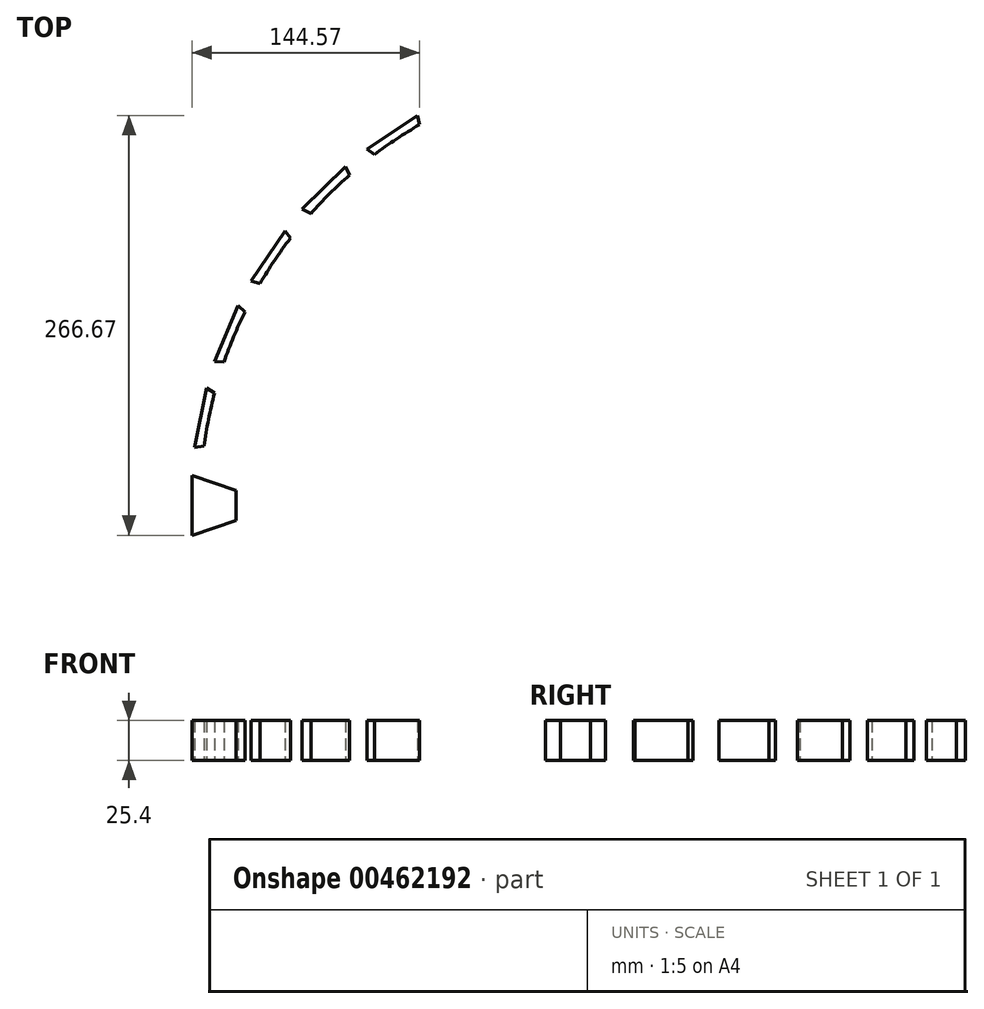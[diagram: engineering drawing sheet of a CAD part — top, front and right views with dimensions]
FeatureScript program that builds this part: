
annotation { "Feature Type Name" : "Feature", "Feature Type Description" : "" }
export const myFeature = defineFeature(function(context is Context, id is Id, definition is map)
    precondition{}
    {
        {
            var Q0;
            Q0=qCreatedBy(makeId("Top.planeOp"),FACE);
            var sketch = newSketch(context, id + "F0", { "sketchPlane" : qUnion([Q0])});
            skCircle(sketch, "E0", {"center": v(0, 0) * mm, "radius": 304.8 * mm});
            skCircle(sketch, "E1", {"center": v(0, 0) * mm, "radius": 279.4 * mm});
            skLineSegment(sketch, "E2", {"start": v(0, 0) * mm, "end": v(-514.18, 0) * mm, "construction": true});
            skLineSegment(sketch, "E3", {"start": v(-256.28, 9.5) * mm, "end": v(-284.48, 19.05) * mm});
            skLineSegment(sketch, "E4.MirrorCS", {"start": v(-256.12, -9.44) * mm, "end": v(-284.48, -19.05) * mm});
            skLineSegment(sketch, "E5", {"start": v(-284.48, 19.05) * mm, "end": v(-284.48, -19.05) * mm});
            skArc(sketch, "E6", {"start": v(-256.36, 9.53) * mm, "mid": v(-256.54, 0) * mm, "end": v(-256.36, -9.53) * mm});
            skLineSegment(sketch, "E7", {"start": v(-249.56, 59.5) * mm, "end": v(-275.26, 74.53) * mm});
            skLineSegment(sketch, "E8.MirrorCS", {"start": v(-253.6, 40.88) * mm, "end": v(-282.7, 36.77) * mm});
            skLineSegment(sketch, "E9", {"start": v(-249.56, 59.5) * mm, "end": v(-253.6, 40.88) * mm});
            skLineSegment(sketch, "E10", {"start": v(-275.26, 74.53) * mm, "end": v(-282.7, 36.77) * mm});
            skLineSegment(sketch, "E11", {"start": v(-278.98, 55.65) * mm, "end": v(0, 0) * mm, "construction": true});
            skLineSegment(sketch, "E12", {"start": v(-233.4, 107.28) * mm, "end": v(-255.29, 126.9) * mm});
            skLineSegment(sketch, "E13.MirrorCS", {"start": v(-240.41, 89.57) * mm, "end": v(-270.13, 91.4) * mm});
            skLineSegment(sketch, "E14", {"start": v(-233.4, 107.28) * mm, "end": v(-240.41, 89.57) * mm});
            skLineSegment(sketch, "E15", {"start": v(-255.29, 126.9) * mm, "end": v(-270.13, 91.4) * mm});
            skLineSegment(sketch, "E16", {"start": v(0, 0) * mm, "end": v(-262.7, 109.15) * mm, "construction": true});
            skLineSegment(sketch, "E17", {"start": v(-207.9, 150.87) * mm, "end": v(-225.53, 174.38) * mm});
            skLineSegment(sketch, "E18.MirrorCS", {"start": v(-218.25, 134.87) * mm, "end": v(-247.03, 142.47) * mm});
            skLineSegment(sketch, "E19", {"start": v(-207.9, 150.87) * mm, "end": v(-218.25, 134.87) * mm});
            skLineSegment(sketch, "E20", {"start": v(-225.53, 174.38) * mm, "end": v(-247.03, 142.47) * mm});
            skLineSegment(sketch, "E21", {"start": v(0, 0) * mm, "end": v(-236.28, 158.43) * mm, "construction": true});
            skLineSegment(sketch, "E22", {"start": v(-251.58, 50.18) * mm, "end": v(0, 0) * mm, "construction": true});
            skLineSegment(sketch, "E23", {"start": v(0, 0) * mm, "end": v(-236.9, 98.43) * mm, "construction": true});
            skLineSegment(sketch, "E24", {"start": v(0, 0) * mm, "end": v(-213.08, 142.87) * mm, "construction": true});
            skLineSegment(sketch, "E25", {"start": v(-174.64, 188.87) * mm, "end": v(-187, 215.06) * mm});
            skLineSegment(sketch, "E26.MirrorCS", {"start": v(-187.38, 174.71) * mm, "end": v(-214.45, 188.13) * mm});
            skLineSegment(sketch, "E27", {"start": v(-174.64, 188.87) * mm, "end": v(-187.38, 174.71) * mm});
            skLineSegment(sketch, "E28", {"start": v(-187, 215.06) * mm, "end": v(-214.45, 188.13) * mm});
            skLineSegment(sketch, "E29", {"start": v(0, 0) * mm, "end": v(-200.73, 201.6) * mm, "construction": true});
            skLineSegment(sketch, "E30", {"start": v(0, 0) * mm, "end": v(-181.01, 181.79) * mm, "construction": true});
            skLineSegment(sketch, "E31", {"start": v(-133.99, 218.9) * mm, "end": v(-141.4, 247.62) * mm});
            skLineSegment(sketch, "E32.MirrorCS", {"start": v(-149.92, 208.46) * mm, "end": v(-173.43, 226.3) * mm});
            skLineSegment(sketch, "E33", {"start": v(-133.99, 218.9) * mm, "end": v(-149.92, 208.46) * mm});
            skLineSegment(sketch, "E34", {"start": v(-141.4, 247.62) * mm, "end": v(-173.43, 226.3) * mm});
            skLineSegment(sketch, "E35", {"start": v(0, 0) * mm, "end": v(-157.41, 236.96) * mm, "construction": true});
            skLineSegment(sketch, "E36", {"start": v(0, 0) * mm, "end": v(-141.95, 213.69) * mm, "construction": true});
            skLineSegment(sketch, "E37", {"start": v(0, 0) * mm, "end": v(-304.8, 0) * mm, "construction": true});
            skPoint(sketch, "E38.orphan", {"position": v(-256.36, 9.53) * mm});
            skPoint(sketch, "E39.orphan", {"position": v(-256.36, -9.53) * mm});
            skArc(sketch, "E40.trimOffspring", {"start": v(-139.42, 215.35) * mm, "mid": v(-140.7, 214.52) * mm, "end": v(-141.95, 213.69) * mm});
            skArc(sketch, "E41.trimOffspring", {"start": v(-249.74, 58.67) * mm, "mid": v(-250.7, 54.43) * mm, "end": v(-251.58, 50.18) * mm});
            skArc(sketch, "E42.trimOffspring", {"start": v(-236.9, 98.43) * mm, "mid": v(-238.54, 94.4) * mm, "end": v(-240.1, 90.36) * mm});
            skArc(sketch, "E43.trimOffspring", {"start": v(-213.08, 142.87) * mm, "mid": v(-215.4, 139.34) * mm, "end": v(-217.67, 135.77) * mm});
            skArc(sketch, "E44.trimOffspring", {"start": v(-181.01, 181.79) * mm, "mid": v(-184.4, 178.36) * mm, "end": v(-187.7, 174.87) * mm});
            skSolve(sketch);
        }
        {
            var Q0;
            Q0=makeQuery(id+"F0.imprint","IMPRINT",FACE,{"disambiguationData":[TD([[makeQuery(id+"F0.imprint","IMPRINT",EDGE,{"derivedFrom":sQuery(id+"F0.wireOp",EDGE,"E0")}),-1.0]])]});
            var Q1;
            {var subQ5=sQuery(id+"F0.wireOp",EDGE,"E20");Q1=makeQuery(id+"F0.imprint","IMPRINT",FACE,{"disambiguationData":[TD([[makeQuery(id+"F0.imprint","IMPRINT",EDGE,{"derivedFrom":subQ5}),1.0]])]});}
            var Q2;
            {var subQ5=sQuery(id+"F0.wireOp",EDGE,"E28");Q2=makeQuery(id+"F0.imprint","IMPRINT",FACE,{"disambiguationData":[TD([[makeQuery(id+"F0.imprint","IMPRINT",EDGE,{"derivedFrom":subQ5}),1.0]])]});}
            var Q3;
            {var subQ5=sQuery(id+"F0.wireOp",EDGE,"E34");Q3=makeQuery(id+"F0.imprint","IMPRINT",FACE,{"disambiguationData":[TD([[makeQuery(id+"F0.imprint","IMPRINT",EDGE,{"derivedFrom":subQ5}),1.0]])]});}
            var Q4;
            {var subQ5=sQuery(id+"F0.wireOp",EDGE,"E15");Q4=makeQuery(id+"F0.imprint","IMPRINT",FACE,{"disambiguationData":[TD([[makeQuery(id+"F0.imprint","IMPRINT",EDGE,{"derivedFrom":subQ5}),1.0]])]});}
            var Q5;
            {var subQ5=sQuery(id+"F0.wireOp",EDGE,"E10");Q5=makeQuery(id+"F0.imprint","IMPRINT",FACE,{"disambiguationData":[TD([[makeQuery(id+"F0.imprint","IMPRINT",EDGE,{"derivedFrom":subQ5}),1.0]])]});}
            var Q6;
            {var subQ5=sQuery(id+"F0.wireOp",EDGE,"E5");Q6=makeQuery(id+"F0.imprint","IMPRINT",FACE,{"disambiguationData":[TD([[makeQuery(id+"F0.imprint","IMPRINT",EDGE,{"derivedFrom":subQ5}),1.0]])]});}
            extrude(context, id + "F1", {"entities" : qUnion([Q0, Q1, Q2, Q3, Q4, Q5, Q6]), "depth" : 25.4 * mm});
        }
        {
            var Q0;
            {var subQ5=sQuery(id+"F0.wireOp",EDGE,"E6");Q0=makeQuery(id+"F0.imprint","IMPRINT",FACE,{"disambiguationData":[TD([[makeQuery(id+"F0.imprint","IMPRINT",EDGE,{"derivedFrom":subQ5}),-1.0]])]});}
            extrude(context, id + "F2", {"entities" : qUnion([Q0]), "operationType" : NewBodyOperationType.ADD, "depth" : 25.4 * mm});
        }
        {
            var Q0;
            {var subQ0=sQuery(id+"F0.wireOp",EDGE,"E6");var subQ1=sQuery(id+"F0.wireOp",EDGE,"E4.MirrorCS");var subQ2=sQuery(id+"F0.wireOp",EDGE,"E3");var subQ3=sQuery(id+"F0.wireOp",EDGE,"E1");Q0=makeQuery(id+"Fd8F3SVLfFubU3N_1.31.F2.boolean.opBoolean","MERGE",FACE,{"derivedFrom":[makeQuery(id+"Fd8F3SVLfFubU3N_1.30.F2.boolean.opBoolean","MERGE",FACE,{"derivedFrom":[makeQuery(id+"Fd8F3SVLfFubU3N_1.29.F2.boolean.opBoolean","MERGE",FACE,{"derivedFrom":[makeQuery(id+"Fd8F3SVLfFubU3N_1.28.F2.boolean.opBoolean","MERGE",FACE,{"derivedFrom":[makeQuery(id+"Fd8F3SVLfFubU3N_1.27.F2.boolean.opBoolean","MERGE",FACE,{"derivedFrom":[makeQuery(id+"Fd8F3SVLfFubU3N_1.26.F2.boolean.opBoolean","MERGE",FACE,{"derivedFrom":[makeQuery(id+"Fd8F3SVLfFubU3N_1.25.F2.boolean.opBoolean","MERGE",FACE,{"derivedFrom":[makeQuery(id+"Fd8F3SVLfFubU3N_1.24.F2.boolean.opBoolean","MERGE",FACE,{"derivedFrom":[makeQuery(id+"Fd8F3SVLfFubU3N_1.23.F2.boolean.opBoolean","MERGE",FACE,{"derivedFrom":[makeQuery(id+"Fd8F3SVLfFubU3N_1.22.F2.boolean.opBoolean","MERGE",FACE,{"derivedFrom":[makeQuery(id+"Fd8F3SVLfFubU3N_1.21.F2.boolean.opBoolean","MERGE",FACE,{"derivedFrom":[makeQuery(id+"Fd8F3SVLfFubU3N_1.20.F2.boolean.opBoolean","MERGE",FACE,{"derivedFrom":[makeQuery(id+"Fd8F3SVLfFubU3N_1.19.F2.boolean.opBoolean","MERGE",FACE,{"derivedFrom":[makeQuery(id+"Fd8F3SVLfFubU3N_1.18.F2.boolean.opBoolean","MERGE",FACE,{"derivedFrom":[makeQuery(id+"Fd8F3SVLfFubU3N_1.17.F2.boolean.opBoolean","MERGE",FACE,{"derivedFrom":[makeQuery(id+"Fd8F3SVLfFubU3N_1.16.F2.boolean.opBoolean","MERGE",FACE,{"derivedFrom":[makeQuery(id+"Fd8F3SVLfFubU3N_1.15.F2.boolean.opBoolean","MERGE",FACE,{"derivedFrom":[makeQuery(id+"Fd8F3SVLfFubU3N_1.14.F2.boolean.opBoolean","MERGE",FACE,{"derivedFrom":[makeQuery(id+"Fd8F3SVLfFubU3N_1.13.F2.boolean.opBoolean","MERGE",FACE,{"derivedFrom":[makeQuery(id+"Fd8F3SVLfFubU3N_1.12.F2.boolean.opBoolean","MERGE",FACE,{"derivedFrom":[makeQuery(id+"Fd8F3SVLfFubU3N_1.11.F2.boolean.opBoolean","MERGE",FACE,{"derivedFrom":[makeQuery(id+"Fd8F3SVLfFubU3N_1.10.F2.boolean.opBoolean","MERGE",FACE,{"derivedFrom":[makeQuery(id+"Fd8F3SVLfFubU3N_1.9.F2.boolean.opBoolean","MERGE",FACE,{"derivedFrom":[makeQuery(id+"Fd8F3SVLfFubU3N_1.8.F2.boolean.opBoolean","MERGE",FACE,{"derivedFrom":[makeQuery(id+"Fd8F3SVLfFubU3N_1.7.F2.boolean.opBoolean","MERGE",FACE,{"derivedFrom":[makeQuery(id+"Fd8F3SVLfFubU3N_1.6.F2.boolean.opBoolean","MERGE",FACE,{"derivedFrom":[makeQuery(id+"Fd8F3SVLfFubU3N_1.5.F2.boolean.opBoolean","MERGE",FACE,{"derivedFrom":[makeQuery(id+"Fd8F3SVLfFubU3N_1.4.F2.boolean.opBoolean","MERGE",FACE,{"derivedFrom":[makeQuery(id+"Fd8F3SVLfFubU3N_1.3.F2.boolean.opBoolean","MERGE",FACE,{"derivedFrom":[makeQuery(id+"Fd8F3SVLfFubU3N_1.2.F2.boolean.opBoolean","MERGE",FACE,{"derivedFrom":[makeQuery(id+"Fd8F3SVLfFubU3N_1.1.F2.boolean.opBoolean","MERGE",FACE,{"derivedFrom":[makeQuery(id+"F2.boolean.opBoolean","MERGE",FACE,{"derivedFrom":[makeQuery(id+"F1.opExtrude","CAP_FACE",FACE,{"disambiguationData":[OSD([subQ3,sQuery(id+"F0.wireOp",EDGE,"E0")])],"isStart":true}),makeQuery(id+"F2.opExtrude","CAP_FACE",FACE,{"disambiguationData":[OSD([subQ3,subQ2,subQ1,subQ0])],"isStart":true})]}),makeQuery(id+"Fd8F3SVLfFubU3N_1.1.F2.opExtrude","CAP_FACE",FACE,{"disambiguationData":[OSD([subQ3,subQ2,subQ1,subQ0])],"isStart":true})]}),makeQuery(id+"Fd8F3SVLfFubU3N_1.2.F2.opExtrude","CAP_FACE",FACE,{"disambiguationData":[OSD([subQ3,subQ2,subQ1,subQ0])],"isStart":true})]}),makeQuery(id+"Fd8F3SVLfFubU3N_1.3.F2.opExtrude","CAP_FACE",FACE,{"disambiguationData":[OSD([subQ3,subQ2,subQ1,subQ0])],"isStart":true})]}),makeQuery(id+"Fd8F3SVLfFubU3N_1.4.F2.opExtrude","CAP_FACE",FACE,{"disambiguationData":[OSD([subQ3,subQ2,subQ1,subQ0])],"isStart":true})]}),makeQuery(id+"Fd8F3SVLfFubU3N_1.5.F2.opExtrude","CAP_FACE",FACE,{"disambiguationData":[OSD([subQ3,subQ2,subQ1,subQ0])],"isStart":true})]}),makeQuery(id+"Fd8F3SVLfFubU3N_1.6.F2.opExtrude","CAP_FACE",FACE,{"disambiguationData":[OSD([subQ3,subQ2,subQ1,subQ0])],"isStart":true})]}),makeQuery(id+"Fd8F3SVLfFubU3N_1.7.F2.opExtrude","CAP_FACE",FACE,{"disambiguationData":[OSD([subQ3,subQ2,subQ1,subQ0])],"isStart":true})]}),makeQuery(id+"Fd8F3SVLfFubU3N_1.8.F2.opExtrude","CAP_FACE",FACE,{"disambiguationData":[OSD([subQ3,subQ2,subQ1,subQ0])],"isStart":true})]}),makeQuery(id+"Fd8F3SVLfFubU3N_1.9.F2.opExtrude","CAP_FACE",FACE,{"disambiguationData":[OSD([subQ3,subQ2,subQ1,subQ0])],"isStart":true})]}),makeQuery(id+"Fd8F3SVLfFubU3N_1.10.F2.opExtrude","CAP_FACE",FACE,{"disambiguationData":[OSD([subQ3,subQ2,subQ1,subQ0])],"isStart":true})]}),makeQuery(id+"Fd8F3SVLfFubU3N_1.11.F2.opExtrude","CAP_FACE",FACE,{"disambiguationData":[OSD([subQ3,subQ2,subQ1,subQ0])],"isStart":true})]}),makeQuery(id+"Fd8F3SVLfFubU3N_1.12.F2.opExtrude","CAP_FACE",FACE,{"disambiguationData":[OSD([subQ3,subQ2,subQ1,subQ0])],"isStart":true})]}),makeQuery(id+"Fd8F3SVLfFubU3N_1.13.F2.opExtrude","CAP_FACE",FACE,{"disambiguationData":[OSD([subQ3,subQ2,subQ1,subQ0])],"isStart":true})]}),makeQuery(id+"Fd8F3SVLfFubU3N_1.14.F2.opExtrude","CAP_FACE",FACE,{"disambiguationData":[OSD([subQ3,subQ2,subQ1,subQ0])],"isStart":true})]}),makeQuery(id+"Fd8F3SVLfFubU3N_1.15.F2.opExtrude","CAP_FACE",FACE,{"disambiguationData":[OSD([subQ3,subQ2,subQ1,subQ0])],"isStart":true})]}),makeQuery(id+"Fd8F3SVLfFubU3N_1.16.F2.opExtrude","CAP_FACE",FACE,{"disambiguationData":[OSD([subQ3,subQ2,subQ1,subQ0])],"isStart":true})]}),makeQuery(id+"Fd8F3SVLfFubU3N_1.17.F2.opExtrude","CAP_FACE",FACE,{"disambiguationData":[OSD([subQ3,subQ2,subQ1,subQ0])],"isStart":true})]}),makeQuery(id+"Fd8F3SVLfFubU3N_1.18.F2.opExtrude","CAP_FACE",FACE,{"disambiguationData":[OSD([subQ3,subQ2,subQ1,subQ0])],"isStart":true})]}),makeQuery(id+"Fd8F3SVLfFubU3N_1.19.F2.opExtrude","CAP_FACE",FACE,{"disambiguationData":[OSD([subQ3,subQ2,subQ1,subQ0])],"isStart":true})]}),makeQuery(id+"Fd8F3SVLfFubU3N_1.20.F2.opExtrude","CAP_FACE",FACE,{"disambiguationData":[OSD([subQ3,subQ2,subQ1,subQ0])],"isStart":true})]}),makeQuery(id+"Fd8F3SVLfFubU3N_1.21.F2.opExtrude","CAP_FACE",FACE,{"disambiguationData":[OSD([subQ3,subQ2,subQ1,subQ0])],"isStart":true})]}),makeQuery(id+"Fd8F3SVLfFubU3N_1.22.F2.opExtrude","CAP_FACE",FACE,{"disambiguationData":[OSD([subQ3,subQ2,subQ1,subQ0])],"isStart":true})]}),makeQuery(id+"Fd8F3SVLfFubU3N_1.23.F2.opExtrude","CAP_FACE",FACE,{"disambiguationData":[OSD([subQ3,subQ2,subQ1,subQ0])],"isStart":true})]}),makeQuery(id+"Fd8F3SVLfFubU3N_1.24.F2.opExtrude","CAP_FACE",FACE,{"disambiguationData":[OSD([subQ3,subQ2,subQ1,subQ0])],"isStart":true})]}),makeQuery(id+"Fd8F3SVLfFubU3N_1.25.F2.opExtrude","CAP_FACE",FACE,{"disambiguationData":[OSD([subQ3,subQ2,subQ1,subQ0])],"isStart":true})]}),makeQuery(id+"Fd8F3SVLfFubU3N_1.26.F2.opExtrude","CAP_FACE",FACE,{"disambiguationData":[OSD([subQ3,subQ2,subQ1,subQ0])],"isStart":true})]}),makeQuery(id+"Fd8F3SVLfFubU3N_1.27.F2.opExtrude","CAP_FACE",FACE,{"disambiguationData":[OSD([subQ3,subQ2,subQ1,subQ0])],"isStart":true})]}),makeQuery(id+"Fd8F3SVLfFubU3N_1.28.F2.opExtrude","CAP_FACE",FACE,{"disambiguationData":[OSD([subQ3,subQ2,subQ1,subQ0])],"isStart":true})]}),makeQuery(id+"Fd8F3SVLfFubU3N_1.29.F2.opExtrude","CAP_FACE",FACE,{"disambiguationData":[OSD([subQ3,subQ2,subQ1,subQ0])],"isStart":true})]}),makeQuery(id+"Fd8F3SVLfFubU3N_1.30.F2.opExtrude","CAP_FACE",FACE,{"disambiguationData":[OSD([subQ3,subQ2,subQ1,subQ0])],"isStart":true})]}),makeQuery(id+"Fd8F3SVLfFubU3N_1.31.F2.opExtrude","CAP_FACE",FACE,{"disambiguationData":[OSD([subQ3,subQ2,subQ1,subQ0])],"isStart":true})]});}
            var sketch = newSketch(context, id + "F3", { "sketchPlane" : qUnion([Q0])});
            skCircle(sketch, "E45", {"center": v(0, 0) * mm, "radius": 296.86 * mm});
            skCircle(sketch, "E46", {"center": v(0, 0) * mm, "radius": 290.51 * mm});
            skSolve(sketch);
        }
        {
            var Q0;
            Q0=makeQuery(id+"F3.imprint","IMPRINT",FACE,{"disambiguationData":[TD([[makeQuery(id+"F3.imprint","IMPRINT",EDGE,{"derivedFrom":sQuery(id+"F3.wireOp",EDGE,"E45")}),1.0]])]});
            extrude(context, id + "F4", {"entities" : qUnion([Q0]), "operationType" : NewBodyOperationType.REMOVE, "oppositeDirection" : true, "depth" : 2.54 * mm});
        }
        {
            var Q0;
            {var subQ0=sQuery(id+"F0.wireOp",EDGE,"E6");var subQ1=sQuery(id+"F0.wireOp",EDGE,"E4.MirrorCS");var subQ2=sQuery(id+"F0.wireOp",EDGE,"E3");var subQ3=sQuery(id+"F0.wireOp",EDGE,"E1");Q0=makeQuery(id+"Fd8F3SVLfFubU3N_1.31.F2.boolean.opBoolean","MERGE",FACE,{"derivedFrom":[makeQuery(id+"Fd8F3SVLfFubU3N_1.30.F2.boolean.opBoolean","MERGE",FACE,{"derivedFrom":[makeQuery(id+"Fd8F3SVLfFubU3N_1.29.F2.boolean.opBoolean","MERGE",FACE,{"derivedFrom":[makeQuery(id+"Fd8F3SVLfFubU3N_1.28.F2.boolean.opBoolean","MERGE",FACE,{"derivedFrom":[makeQuery(id+"Fd8F3SVLfFubU3N_1.27.F2.boolean.opBoolean","MERGE",FACE,{"derivedFrom":[makeQuery(id+"Fd8F3SVLfFubU3N_1.26.F2.boolean.opBoolean","MERGE",FACE,{"derivedFrom":[makeQuery(id+"Fd8F3SVLfFubU3N_1.25.F2.boolean.opBoolean","MERGE",FACE,{"derivedFrom":[makeQuery(id+"Fd8F3SVLfFubU3N_1.24.F2.boolean.opBoolean","MERGE",FACE,{"derivedFrom":[makeQuery(id+"Fd8F3SVLfFubU3N_1.23.F2.boolean.opBoolean","MERGE",FACE,{"derivedFrom":[makeQuery(id+"Fd8F3SVLfFubU3N_1.22.F2.boolean.opBoolean","MERGE",FACE,{"derivedFrom":[makeQuery(id+"Fd8F3SVLfFubU3N_1.21.F2.boolean.opBoolean","MERGE",FACE,{"derivedFrom":[makeQuery(id+"Fd8F3SVLfFubU3N_1.20.F2.boolean.opBoolean","MERGE",FACE,{"derivedFrom":[makeQuery(id+"Fd8F3SVLfFubU3N_1.19.F2.boolean.opBoolean","MERGE",FACE,{"derivedFrom":[makeQuery(id+"Fd8F3SVLfFubU3N_1.18.F2.boolean.opBoolean","MERGE",FACE,{"derivedFrom":[makeQuery(id+"Fd8F3SVLfFubU3N_1.17.F2.boolean.opBoolean","MERGE",FACE,{"derivedFrom":[makeQuery(id+"Fd8F3SVLfFubU3N_1.16.F2.boolean.opBoolean","MERGE",FACE,{"derivedFrom":[makeQuery(id+"Fd8F3SVLfFubU3N_1.15.F2.boolean.opBoolean","MERGE",FACE,{"derivedFrom":[makeQuery(id+"Fd8F3SVLfFubU3N_1.14.F2.boolean.opBoolean","MERGE",FACE,{"derivedFrom":[makeQuery(id+"Fd8F3SVLfFubU3N_1.13.F2.boolean.opBoolean","MERGE",FACE,{"derivedFrom":[makeQuery(id+"Fd8F3SVLfFubU3N_1.12.F2.boolean.opBoolean","MERGE",FACE,{"derivedFrom":[makeQuery(id+"Fd8F3SVLfFubU3N_1.11.F2.boolean.opBoolean","MERGE",FACE,{"derivedFrom":[makeQuery(id+"Fd8F3SVLfFubU3N_1.10.F2.boolean.opBoolean","MERGE",FACE,{"derivedFrom":[makeQuery(id+"Fd8F3SVLfFubU3N_1.9.F2.boolean.opBoolean","MERGE",FACE,{"derivedFrom":[makeQuery(id+"Fd8F3SVLfFubU3N_1.8.F2.boolean.opBoolean","MERGE",FACE,{"derivedFrom":[makeQuery(id+"Fd8F3SVLfFubU3N_1.7.F2.boolean.opBoolean","MERGE",FACE,{"derivedFrom":[makeQuery(id+"Fd8F3SVLfFubU3N_1.6.F2.boolean.opBoolean","MERGE",FACE,{"derivedFrom":[makeQuery(id+"Fd8F3SVLfFubU3N_1.5.F2.boolean.opBoolean","MERGE",FACE,{"derivedFrom":[makeQuery(id+"Fd8F3SVLfFubU3N_1.4.F2.boolean.opBoolean","MERGE",FACE,{"derivedFrom":[makeQuery(id+"Fd8F3SVLfFubU3N_1.3.F2.boolean.opBoolean","MERGE",FACE,{"derivedFrom":[makeQuery(id+"Fd8F3SVLfFubU3N_1.2.F2.boolean.opBoolean","MERGE",FACE,{"derivedFrom":[makeQuery(id+"Fd8F3SVLfFubU3N_1.1.F2.boolean.opBoolean","MERGE",FACE,{"derivedFrom":[makeQuery(id+"F2.boolean.opBoolean","MERGE",FACE,{"derivedFrom":[makeQuery(id+"F1.opExtrude","CAP_FACE",FACE,{"disambiguationData":[OSD([subQ3,sQuery(id+"F0.wireOp",EDGE,"E0")])],"isStart":false}),makeQuery(id+"F2.opExtrude","CAP_FACE",FACE,{"disambiguationData":[OSD([subQ3,subQ2,subQ1,subQ0])],"isStart":false})]}),makeQuery(id+"Fd8F3SVLfFubU3N_1.1.F2.opExtrude","CAP_FACE",FACE,{"disambiguationData":[OSD([subQ3,subQ2,subQ1,subQ0])],"isStart":false})]}),makeQuery(id+"Fd8F3SVLfFubU3N_1.2.F2.opExtrude","CAP_FACE",FACE,{"disambiguationData":[OSD([subQ3,subQ2,subQ1,subQ0])],"isStart":false})]}),makeQuery(id+"Fd8F3SVLfFubU3N_1.3.F2.opExtrude","CAP_FACE",FACE,{"disambiguationData":[OSD([subQ3,subQ2,subQ1,subQ0])],"isStart":false})]}),makeQuery(id+"Fd8F3SVLfFubU3N_1.4.F2.opExtrude","CAP_FACE",FACE,{"disambiguationData":[OSD([subQ3,subQ2,subQ1,subQ0])],"isStart":false})]}),makeQuery(id+"Fd8F3SVLfFubU3N_1.5.F2.opExtrude","CAP_FACE",FACE,{"disambiguationData":[OSD([subQ3,subQ2,subQ1,subQ0])],"isStart":false})]}),makeQuery(id+"Fd8F3SVLfFubU3N_1.6.F2.opExtrude","CAP_FACE",FACE,{"disambiguationData":[OSD([subQ3,subQ2,subQ1,subQ0])],"isStart":false})]}),makeQuery(id+"Fd8F3SVLfFubU3N_1.7.F2.opExtrude","CAP_FACE",FACE,{"disambiguationData":[OSD([subQ3,subQ2,subQ1,subQ0])],"isStart":false})]}),makeQuery(id+"Fd8F3SVLfFubU3N_1.8.F2.opExtrude","CAP_FACE",FACE,{"disambiguationData":[OSD([subQ3,subQ2,subQ1,subQ0])],"isStart":false})]}),makeQuery(id+"Fd8F3SVLfFubU3N_1.9.F2.opExtrude","CAP_FACE",FACE,{"disambiguationData":[OSD([subQ3,subQ2,subQ1,subQ0])],"isStart":false})]}),makeQuery(id+"Fd8F3SVLfFubU3N_1.10.F2.opExtrude","CAP_FACE",FACE,{"disambiguationData":[OSD([subQ3,subQ2,subQ1,subQ0])],"isStart":false})]}),makeQuery(id+"Fd8F3SVLfFubU3N_1.11.F2.opExtrude","CAP_FACE",FACE,{"disambiguationData":[OSD([subQ3,subQ2,subQ1,subQ0])],"isStart":false})]}),makeQuery(id+"Fd8F3SVLfFubU3N_1.12.F2.opExtrude","CAP_FACE",FACE,{"disambiguationData":[OSD([subQ3,subQ2,subQ1,subQ0])],"isStart":false})]}),makeQuery(id+"Fd8F3SVLfFubU3N_1.13.F2.opExtrude","CAP_FACE",FACE,{"disambiguationData":[OSD([subQ3,subQ2,subQ1,subQ0])],"isStart":false})]}),makeQuery(id+"Fd8F3SVLfFubU3N_1.14.F2.opExtrude","CAP_FACE",FACE,{"disambiguationData":[OSD([subQ3,subQ2,subQ1,subQ0])],"isStart":false})]}),makeQuery(id+"Fd8F3SVLfFubU3N_1.15.F2.opExtrude","CAP_FACE",FACE,{"disambiguationData":[OSD([subQ3,subQ2,subQ1,subQ0])],"isStart":false})]}),makeQuery(id+"Fd8F3SVLfFubU3N_1.16.F2.opExtrude","CAP_FACE",FACE,{"disambiguationData":[OSD([subQ3,subQ2,subQ1,subQ0])],"isStart":false})]}),makeQuery(id+"Fd8F3SVLfFubU3N_1.17.F2.opExtrude","CAP_FACE",FACE,{"disambiguationData":[OSD([subQ3,subQ2,subQ1,subQ0])],"isStart":false})]}),makeQuery(id+"Fd8F3SVLfFubU3N_1.18.F2.opExtrude","CAP_FACE",FACE,{"disambiguationData":[OSD([subQ3,subQ2,subQ1,subQ0])],"isStart":false})]}),makeQuery(id+"Fd8F3SVLfFubU3N_1.19.F2.opExtrude","CAP_FACE",FACE,{"disambiguationData":[OSD([subQ3,subQ2,subQ1,subQ0])],"isStart":false})]}),makeQuery(id+"Fd8F3SVLfFubU3N_1.20.F2.opExtrude","CAP_FACE",FACE,{"disambiguationData":[OSD([subQ3,subQ2,subQ1,subQ0])],"isStart":false})]}),makeQuery(id+"Fd8F3SVLfFubU3N_1.21.F2.opExtrude","CAP_FACE",FACE,{"disambiguationData":[OSD([subQ3,subQ2,subQ1,subQ0])],"isStart":false})]}),makeQuery(id+"Fd8F3SVLfFubU3N_1.22.F2.opExtrude","CAP_FACE",FACE,{"disambiguationData":[OSD([subQ3,subQ2,subQ1,subQ0])],"isStart":false})]}),makeQuery(id+"Fd8F3SVLfFubU3N_1.23.F2.opExtrude","CAP_FACE",FACE,{"disambiguationData":[OSD([subQ3,subQ2,subQ1,subQ0])],"isStart":false})]}),makeQuery(id+"Fd8F3SVLfFubU3N_1.24.F2.opExtrude","CAP_FACE",FACE,{"disambiguationData":[OSD([subQ3,subQ2,subQ1,subQ0])],"isStart":false})]}),makeQuery(id+"Fd8F3SVLfFubU3N_1.25.F2.opExtrude","CAP_FACE",FACE,{"disambiguationData":[OSD([subQ3,subQ2,subQ1,subQ0])],"isStart":false})]}),makeQuery(id+"Fd8F3SVLfFubU3N_1.26.F2.opExtrude","CAP_FACE",FACE,{"disambiguationData":[OSD([subQ3,subQ2,subQ1,subQ0])],"isStart":false})]}),makeQuery(id+"Fd8F3SVLfFubU3N_1.27.F2.opExtrude","CAP_FACE",FACE,{"disambiguationData":[OSD([subQ3,subQ2,subQ1,subQ0])],"isStart":false})]}),makeQuery(id+"Fd8F3SVLfFubU3N_1.28.F2.opExtrude","CAP_FACE",FACE,{"disambiguationData":[OSD([subQ3,subQ2,subQ1,subQ0])],"isStart":false})]}),makeQuery(id+"Fd8F3SVLfFubU3N_1.29.F2.opExtrude","CAP_FACE",FACE,{"disambiguationData":[OSD([subQ3,subQ2,subQ1,subQ0])],"isStart":false})]}),makeQuery(id+"Fd8F3SVLfFubU3N_1.30.F2.opExtrude","CAP_FACE",FACE,{"disambiguationData":[OSD([subQ3,subQ2,subQ1,subQ0])],"isStart":false})]}),makeQuery(id+"Fd8F3SVLfFubU3N_1.31.F2.opExtrude","CAP_FACE",FACE,{"disambiguationData":[OSD([subQ3,subQ2,subQ1,subQ0])],"isStart":false})]});}
            var sketch = newSketch(context, id + "F5", { "sketchPlane" : qUnion([Q0])});
            skCircle(sketch, "E47", {"center": v(0, 0) * mm, "radius": 296.86 * mm});
            skCircle(sketch, "E48", {"center": v(0, 0) * mm, "radius": 290.51 * mm});
            skSolve(sketch);
        }
        {
            var Q0;
            Q0=makeQuery(id+"F5.imprint","IMPRINT",FACE,{"disambiguationData":[TD([[makeQuery(id+"F5.imprint","IMPRINT",EDGE,{"derivedFrom":sQuery(id+"F5.wireOp",EDGE,"E47")}),1.0]])]});
            extrude(context, id + "F6", {"entities" : qUnion([Q0]), "operationType" : NewBodyOperationType.REMOVE, "oppositeDirection" : true, "depth" : 2.54 * mm});
        }
    });
